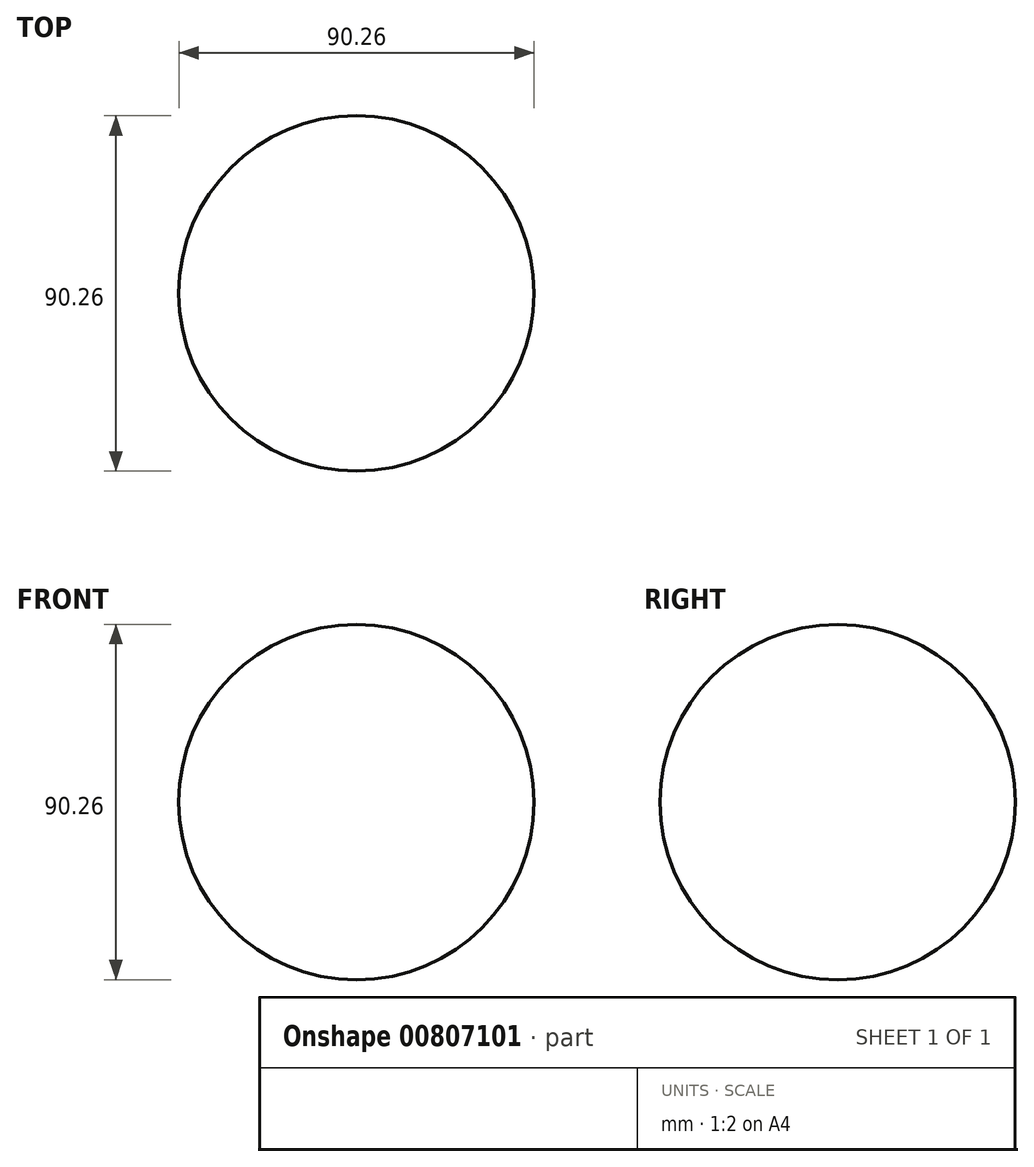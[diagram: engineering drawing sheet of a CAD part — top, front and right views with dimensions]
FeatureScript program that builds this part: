
annotation { "Feature Type Name" : "Feature", "Feature Type Description" : "" }
export const myFeature = defineFeature(function(context is Context, id is Id, definition is map)
    precondition{}
    {
        {
            var Q0;
            Q0=qCreatedBy(makeId("Front.planeOp"),FACE);
            var sketch = newSketch(context, id + "F0", { "sketchPlane" : qUnion([Q0])});
            skCircle(sketch, "E0", {"center": v(0, 0) * mm, "radius": 45.13 * mm});
            skLineSegment(sketch, "E1", {"start": v(0, 73.27) * mm, "end": v(0, -73.04) * mm});
            skSolve(sketch);
        }
        {
            var Q0;
            {var subQ0=sQuery(id+"F0.wireOp",EDGE,"E1");var subQ1=sQuery(id+"F0.wireOp",EDGE,"E0");var subQ2=makeQuery(id+"F0.imprint","INTERSECT",VERTEX,{"disambiguationData":[OD(0.0)],"derivedFrom":[subQ1,subQ0]});Q0=makeQuery(id+"F0.imprint","IMPRINT",FACE,{"disambiguationData":[TD([[makeQuery(id+"F0.imprint","IMPRINT",EDGE,{"disambiguationData":[TD([[subQ2,-1.0]])],"derivedFrom":subQ1}),1.0]])]});}
            var Q1;
            Q1=sQuery(id+"F0.wireOp",EDGE,"E1");
            revolve(context, id + "F1", {"surfaceOperationType" : NewSurfaceOperationType.NEW, "entities" : qUnion([Q0]), "axis" : qUnion([Q1]), "revolveType" : RevolveType.FULL});
        }
    });
